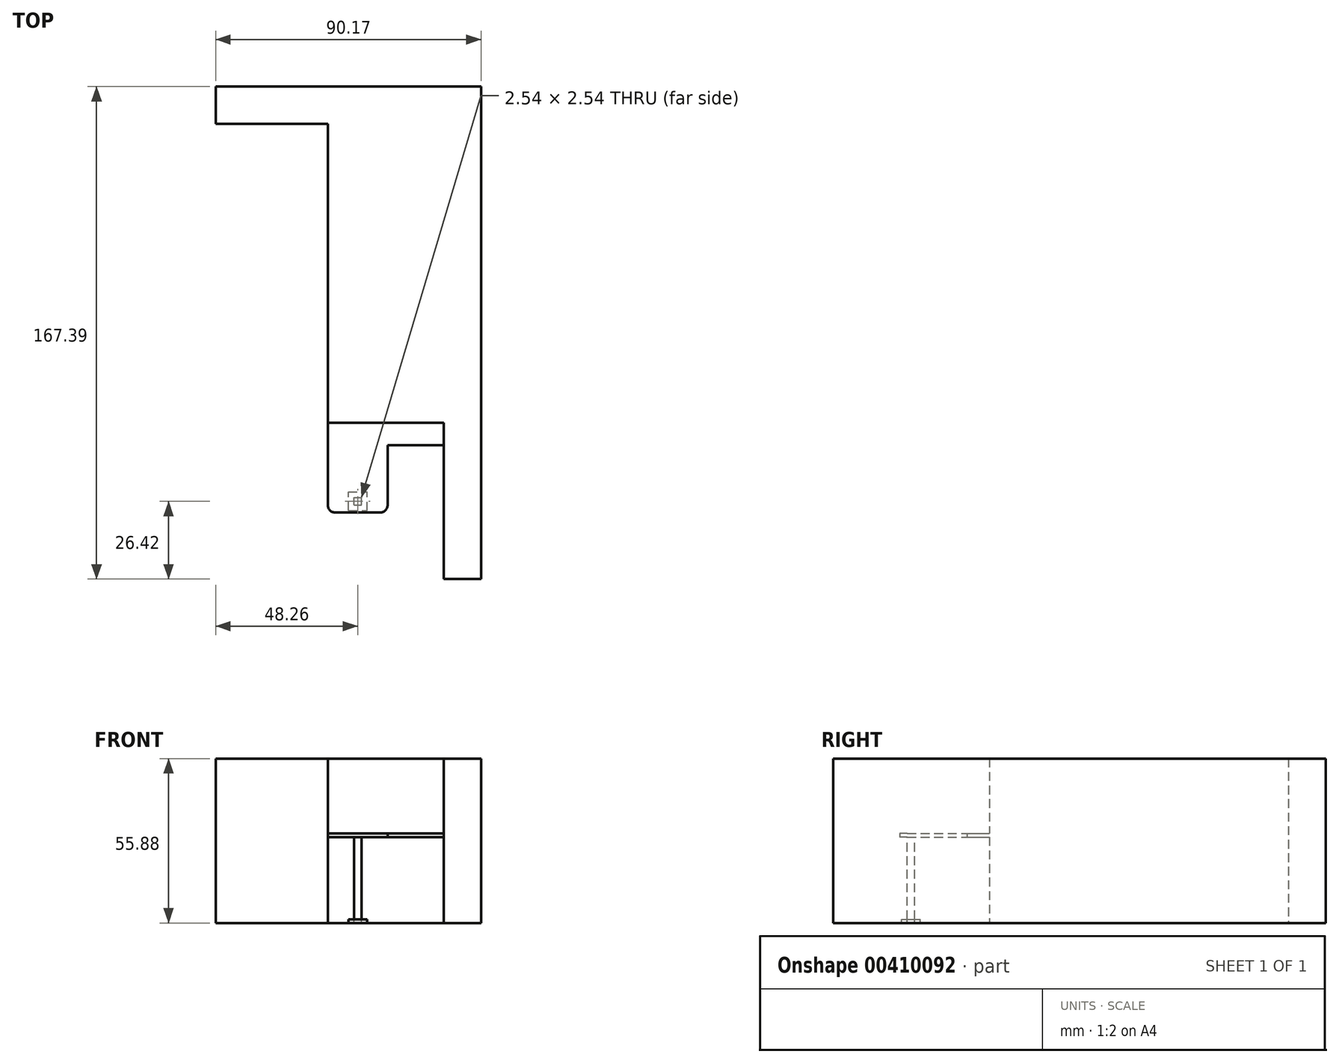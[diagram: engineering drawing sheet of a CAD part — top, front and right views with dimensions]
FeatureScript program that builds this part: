
annotation { "Feature Type Name" : "Feature", "Feature Type Description" : "" }
export const myFeature = defineFeature(function(context is Context, id is Id, definition is map)
    precondition{}
    {
        {
            var Q0;
            Q0=qCreatedBy(makeId("Top.planeOp"),FACE);
            var sketch = newSketch(context, id + "F0", { "sketchPlane" : qUnion([Q0])});
            skLineSegment(sketch, "E0", {"start": v(0, 0) * mm, "end": v(0, 101.6) * mm});
            skLineSegment(sketch, "E1", {"start": v(0, 101.6) * mm, "end": v(-38.1, 101.6) * mm});
            skLineSegment(sketch, "E2", {"start": v(0, 0) * mm, "end": v(39.37, 0) * mm});
            skLineSegment(sketch, "E3", {"start": v(39.37, 0) * mm, "end": v(39.37, -53.09) * mm});
            skLineSegment(sketch, "E4", {"start": v(39.37, -53.09) * mm, "end": v(52.07, -53.09) * mm});
            skLineSegment(sketch, "E5", {"start": v(52.07, -53.09) * mm, "end": v(52.07, 114.3) * mm});
            skLineSegment(sketch, "E6", {"start": v(52.07, 114.3) * mm, "end": v(-38.1, 114.3) * mm});
            skLineSegment(sketch, "E7", {"start": v(-38.1, 101.6) * mm, "end": v(-38.1, 114.3) * mm});
            skSolve(sketch);
        }
        {
            var Q0;
            Q0=makeQuery(id+"F0.imprint","IMPRINT",FACE,{"disambiguationData":[TD([[makeQuery(id+"F0.imprint","IMPRINT",EDGE,{"derivedFrom":sQuery(id+"F0.wireOp",EDGE,"E0")}),-1.0]])]});
            extrude(context, id + "F1", {"entities" : qUnion([Q0]), "depth" : 55.88 * mm});
        }
        {
            var Q0;
            Q0=makeQuery(id+"F1.opExtrude","SWEPT_FACE",FACE,{"disambiguationData":[OSD([sQuery(id+"F0.wireOp",EDGE,"E2")])]});
            var sketch = newSketch(context, id + "F2", { "sketchPlane" : qUnion([Q0])});
            skLineSegment(sketch, "E8.bottom", {"start": v(39.37, 29.21) * mm, "end": v(0, 29.21) * mm});
            skLineSegment(sketch, "E8.top", {"start": v(39.37, 30.48) * mm, "end": v(0, 30.48) * mm});
            skLineSegment(sketch, "E8.left", {"start": v(39.37, 29.21) * mm, "end": v(39.37, 30.48) * mm});
            skLineSegment(sketch, "E8.right", {"start": v(0, 29.21) * mm, "end": v(0, 30.48) * mm});
            skSolve(sketch);
        }
        {
            var Q0;
            Q0=makeQuery(id+"F2.imprint","IMPRINT",FACE,{"disambiguationData":[TD([[makeQuery(id+"F2.imprint","IMPRINT",EDGE,{"derivedFrom":sQuery(id+"F2.wireOp",EDGE,"E8.bottom")}),-1.0]])]});
            extrude(context, id + "F3", {"entities" : qUnion([Q0]), "operationType" : NewBodyOperationType.ADD, "depth" : 7.62 * mm});
        }
        {
            var Q0;
            Q0=makeQuery(id+"F3.opExtrude","CAP_FACE",FACE,{"disambiguationData":[OSD([sQuery(id+"F2.wireOp",EDGE,"E8.bottom"),sQuery(id+"F2.wireOp",EDGE,"E8.top"),sQuery(id+"F2.wireOp",EDGE,"E8.left"),sQuery(id+"F2.wireOp",EDGE,"E8.right")])],"isStart":false});
            var sketch = newSketch(context, id + "F4", { "sketchPlane" : qUnion([Q0])});
            skLineSegment(sketch, "E9.bottom", {"start": v(0, 30.48) * mm, "end": v(20.32, 30.48) * mm});
            skLineSegment(sketch, "E9.top", {"start": v(0, 29.21) * mm, "end": v(20.32, 29.21) * mm});
            skLineSegment(sketch, "E9.left", {"start": v(0, 30.48) * mm, "end": v(0, 29.21) * mm});
            skLineSegment(sketch, "E9.right", {"start": v(20.32, 30.48) * mm, "end": v(20.32, 29.21) * mm});
            skSolve(sketch);
        }
        {
            var Q0;
            Q0=makeQuery(id+"F4.imprint","IMPRINT",FACE,{"disambiguationData":[TD([[makeQuery(id+"F4.imprint","IMPRINT",EDGE,{"derivedFrom":sQuery(id+"F4.wireOp",EDGE,"E9.bottom")}),1.0]])]});
            extrude(context, id + "F5", {"entities" : qUnion([Q0]), "operationType" : NewBodyOperationType.ADD, "depth" : 22.86 * mm});
        }
        {
            var Q0;
            Q0=makeQuery(id+"F5.opExtrude","CAP_EDGE",EDGE,{"disambiguationData":[OSD([sQuery(id+"F4.wireOp",EDGE,"E9.left")])],"isStart":false});
            var Q1;
            Q1=makeQuery(id+"F5.opExtrude","CAP_EDGE",EDGE,{"disambiguationData":[OSD([sQuery(id+"F4.wireOp",EDGE,"E9.right")])],"isStart":false});
            fillet(context, id + "F6", {"entities" : qUnion([Q0, Q1]), "radius" : 2.54 * mm, "tangentPropagation" : true, "allowEdgeOverflow" : false});
        }
        {
            var Q0;
            Q0=makeQuery(id+"F5.boolean.opBoolean","MERGE",FACE,{"derivedFrom":[makeQuery(id+"F3.opExtrude","SWEPT_FACE",FACE,{"disambiguationData":[OSD([sQuery(id+"F2.wireOp",EDGE,"E8.bottom")])]}),makeQuery(id+"F5.opExtrude","SWEPT_FACE",FACE,{"disambiguationData":[OSD([sQuery(id+"F4.wireOp",EDGE,"E9.top")])]})]});
            var sketch = newSketch(context, id + "F7", { "sketchPlane" : qUnion([Q0])});
            skLineSegment(sketch, "E10.bottom", {"start": v(8.9, 27.94) * mm, "end": v(11.43, 27.94) * mm});
            skLineSegment(sketch, "E10.top", {"start": v(8.9, 25.4) * mm, "end": v(11.43, 25.4) * mm});
            skLineSegment(sketch, "E10.left", {"start": v(8.9, 27.94) * mm, "end": v(8.9, 25.4) * mm});
            skLineSegment(sketch, "E10.right", {"start": v(11.43, 27.94) * mm, "end": v(11.43, 25.4) * mm});
            skPoint(sketch, "E10.middle", {"position": v(10.16, 26.67) * mm});
            skSolve(sketch);
        }
        {
            var Q0;
            Q0=makeQuery(id+"F7.imprint","IMPRINT",FACE,{"disambiguationData":[TD([[makeQuery(id+"F7.imprint","IMPRINT",EDGE,{"derivedFrom":sQuery(id+"F7.wireOp",EDGE,"E10.bottom")}),-1.0]])]});
            extrude(context, id + "F8", {"entities" : qUnion([Q0]), "operationType" : NewBodyOperationType.ADD, "depth" : 27.94 * mm});
        }
        {
            var Q0;
            Q0=makeQuery(id+"F8.opExtrude","CAP_FACE",FACE,{"disambiguationData":[OSD([sQuery(id+"F7.wireOp",EDGE,"E10.bottom"),sQuery(id+"F7.wireOp",EDGE,"E10.top"),sQuery(id+"F7.wireOp",EDGE,"E10.left"),sQuery(id+"F7.wireOp",EDGE,"E10.right")])],"isStart":false});
            var sketch = newSketch(context, id + "F9", { "sketchPlane" : qUnion([Q0])});
            skLineSegment(sketch, "E11.bottom", {"start": v(6.99, 29.84) * mm, "end": v(13.34, 29.84) * mm});
            skLineSegment(sketch, "E11.top", {"start": v(6.99, 23.5) * mm, "end": v(13.34, 23.5) * mm});
            skLineSegment(sketch, "E11.left", {"start": v(6.99, 29.84) * mm, "end": v(6.99, 23.5) * mm});
            skLineSegment(sketch, "E11.right", {"start": v(13.34, 29.84) * mm, "end": v(13.34, 23.5) * mm});
            skPoint(sketch, "E11.middle", {"position": v(10.16, 26.67) * mm});
            skSolve(sketch);
        }
        {
            var Q0;
            Q0=makeQuery(id+"F9.imprint","IMPRINT",FACE,{"disambiguationData":[TD([[makeQuery(id+"F9.imprint","IMPRINT",EDGE,{"derivedFrom":sQuery(id+"F9.wireOp",EDGE,"E11.bottom")}),-1.0]])]});
            extrude(context, id + "F10", {"entities" : qUnion([Q0]), "depth" : 1.27 * mm});
        }
    });
